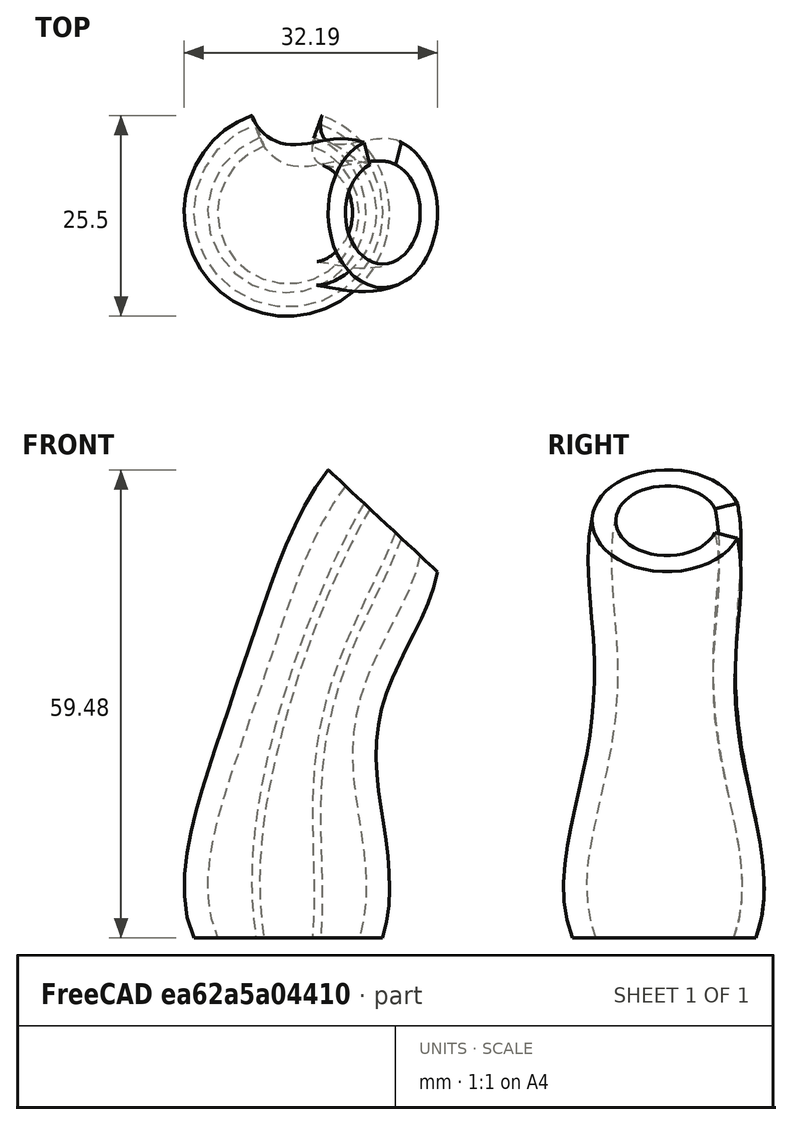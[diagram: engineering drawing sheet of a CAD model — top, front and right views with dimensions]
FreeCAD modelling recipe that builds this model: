
FCSTD DOCUMENT  (FreeCAD 0.16R6706 (Git))
Label: Suporte Fiacao Sensor
License: All rights reserved
LicenseURL: http://en.wikipedia.org/wiki/All_rights_reserved
objects: Sketcher::SketchObject×5, Part::Loft×1
note: 6 computed .brp shape members not serialized (recipe doc carries the construction recipe); baked Part::Feature solids carry a one-line shape summary decoded from their .brp

FEATURE [Sketcher::SketchObject] Sketch  label="base"
  sketch-geometry (5):
    g0: ArcOfCircle CenterX=0 CenterY=0 CenterZ=0 NormalX=0 NormalY=0 NormalZ=1 Radius=9 StartAngle=1.91986 EndAngle=7.50492
    g1: ArcOfCircle CenterX=0 CenterY=0 CenterZ=0 NormalX=0 NormalY=0 NormalZ=1 Radius=12 StartAngle=1.91986 EndAngle=7.50492
    g2: LineSegment StartX=-4.10424 StartY=11.2763 StartZ=0 EndX=-3.07818 EndY=8.45723 EndZ=0
    g3: LineSegment StartX=3.07818 StartY=8.45723 StartZ=0 EndX=4.10424 EndY=11.2763 EndZ=0
    g4: LineSegment [constr] StartX=0 StartY=11.3802 StartZ=0 EndX=0 EndY=0 EndZ=0
  constraints (14):
    c: Coincident(g0,g1)
    c: Coincident(g0,g-1)
    c: Radius(g0) = 9
    c: Radius(g1) = 12
    c: Angle(g0) = 5.58505
    c: Angle(g2) = -1.22173
    c: Angle(g3) = 1.22173
    c: Coincident(g3,g0)
    c: Coincident(g1,g3)
    c: Coincident(g0,g2)
    c: Coincident(g1,g2)
    c: Vertical(g4)
    c: Coincident(g4,g-1)
    c: Symmetric(g0,g0,g4)
FEATURE [Sketcher::SketchObject] Sketch001  label="base001"
  Placement = pos=(0,0,15) rot=(0,0,1;0rad)
  sketch-geometry (5):
    g0: ArcOfCircle CenterX=0 CenterY=0 CenterZ=0 NormalX=0 NormalY=0 NormalZ=1 Radius=9 StartAngle=1.91986 EndAngle=7.50492
    g1: ArcOfCircle CenterX=0 CenterY=0 CenterZ=0 NormalX=0 NormalY=0 NormalZ=1 Radius=12 StartAngle=1.91986 EndAngle=7.50492
    g2: LineSegment StartX=-4.10424 StartY=11.2763 StartZ=0 EndX=-3.07818 EndY=8.45723 EndZ=0
    g3: LineSegment StartX=3.07818 StartY=8.45723 StartZ=0 EndX=4.10424 EndY=11.2763 EndZ=0
    g4: LineSegment [constr] StartX=0 StartY=35.9116 StartZ=0 EndX=0 EndY=0 EndZ=0
  constraints (14):
    c: Coincident(g0,g1)
    c: Coincident(g0,g-1)
    c: Radius(g0) = 9
    c: Radius(g1) = 12
    c: Angle(g0) = 5.58505
    c: Angle(g2) = -1.22173
    c: Angle(g3) = 1.22173
    c: Coincident(g3,g0)
    c: Coincident(g1,g3)
    c: Coincident(g0,g2)
    c: Coincident(g1,g2)
    c: Vertical(g4)
    c: Coincident(g4,g-1)
    c: Symmetric(g0,g0,g4)
FEATURE [Sketcher::SketchObject] Sketch002  label="base002"
  Placement = pos=(2,0,28) rot=(0,1,0;0.20944rad)
  sketch-geometry (5):
    g0: ArcOfCircle CenterX=0 CenterY=0 CenterZ=0 NormalX=0 NormalY=0 NormalZ=1 Radius=6.5 StartAngle=1.91986 EndAngle=7.50492
    g1: ArcOfCircle CenterX=0 CenterY=0 CenterZ=0 NormalX=0 NormalY=0 NormalZ=1 Radius=9.5 StartAngle=1.91986 EndAngle=7.50492
    g2: LineSegment StartX=-3.24919 StartY=8.92708 StartZ=0 EndX=-2.22313 EndY=6.108 EndZ=0
    g3: LineSegment StartX=2.22313 StartY=6.108 StartZ=0 EndX=3.24919 EndY=8.92708 EndZ=0
    g4: LineSegment [constr] StartX=0 StartY=34.3816 StartZ=0 EndX=0 EndY=0 EndZ=0
  constraints (14):
    c: Coincident(g0,g1)
    c: Coincident(g0,g-1)
    c: Radius(g0) = 6.5
    c: Radius(g1) = 9.5
    c: Angle(g0) = 5.58505
    c: Angle(g2) = -1.22173
    c: Angle(g3) = 1.22173
    c: Coincident(g3,g0)
    c: Coincident(g1,g3)
    c: Coincident(g0,g2)
    c: Coincident(g1,g2)
    c: Vertical(g4)
    c: Coincident(g4,g-1)
    c: Symmetric(g0,g0,g4)
FEATURE [Sketcher::SketchObject] Sketch003  label="base003"
  Placement = pos=(6,0,40) rot=(0,1,0;0.506145rad)
  sketch-geometry (5):
    g0: ArcOfCircle CenterX=0 CenterY=0 CenterZ=0 NormalX=0 NormalY=0 NormalZ=1 Radius=6.5 StartAngle=1.91986 EndAngle=7.50492
    g1: ArcOfCircle CenterX=0 CenterY=0 CenterZ=0 NormalX=0 NormalY=0 NormalZ=1 Radius=9.5 StartAngle=1.91986 EndAngle=7.50492
    g2: LineSegment StartX=-3.24919 StartY=8.92708 StartZ=0 EndX=-2.22313 EndY=6.108 EndZ=0
    g3: LineSegment StartX=2.22313 StartY=6.108 StartZ=0 EndX=3.24919 EndY=8.92708 EndZ=0
    g4: LineSegment [constr] StartX=0 StartY=17.1016 StartZ=0 EndX=0 EndY=0 EndZ=0
  constraints (14):
    c: Coincident(g0,g1)
    c: Coincident(g0,g-1)
    c: Radius(g0) = 6.5
    c: Radius(g1) = 9.5
    c: Angle(g0) = 5.58505
    c: Angle(g2) = -1.22173
    c: Angle(g3) = 1.22173
    c: Coincident(g3,g0)
    c: Coincident(g1,g3)
    c: Coincident(g0,g2)
    c: Coincident(g1,g2)
    c: Vertical(g4)
    c: Coincident(g4,g-1)
    c: Symmetric(g0,g0,g4)
FEATURE [Sketcher::SketchObject] Sketch004  label="base004"
  Placement = pos=(12,0,53) rot=(0,1,0;0.750492rad)
  sketch-geometry (5):
    g0: ArcOfCircle CenterX=0 CenterY=0 CenterZ=0 NormalX=0 NormalY=0 NormalZ=1 Radius=6.5 StartAngle=1.91986 EndAngle=7.50492
    g1: ArcOfCircle CenterX=0 CenterY=0 CenterZ=0 NormalX=0 NormalY=0 NormalZ=1 Radius=9.5 StartAngle=1.91986 EndAngle=7.50492
    g2: LineSegment StartX=-3.24919 StartY=8.92708 StartZ=0 EndX=-2.22313 EndY=6.108 EndZ=0
    g3: LineSegment StartX=2.22313 StartY=6.108 StartZ=0 EndX=3.24919 EndY=8.92708 EndZ=0
    g4: LineSegment [constr] StartX=0 StartY=33.4637 StartZ=0 EndX=0 EndY=0 EndZ=0
  constraints (14):
    c: Coincident(g0,g1)
    c: Coincident(g0,g-1)
    c: Radius(g0) = 6.5
    c: Radius(g1) = 9.5
    c: Angle(g0) = 5.58505
    c: Angle(g2) = -1.22173
    c: Angle(g3) = 1.22173
    c: Coincident(g3,g0)
    c: Coincident(g1,g3)
    c: Coincident(g0,g2)
    c: Coincident(g1,g2)
    c: Vertical(g4)
    c: Coincident(g-1,g4)
    c: Symmetric(g0,g0,g4)
FEATURE [Part::Loft] Loft
  Closed = false
  Ruled = false
  Sections = -> [Sketch004,Sketch003,Sketch002,Sketch001,Sketch]
  Solid = true
